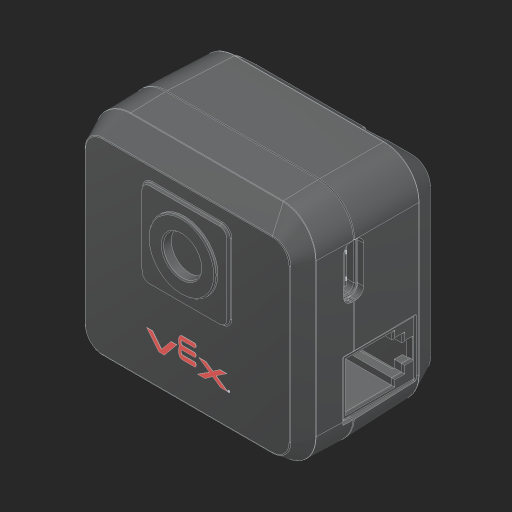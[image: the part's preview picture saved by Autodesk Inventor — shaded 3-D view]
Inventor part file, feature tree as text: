
AUTODESK INVENTOR PART (.ipt)
format: ipt  version: 2023 (Build 270158000, 158)  size: 2,909,696 bytes
history: native  units: in
note: dims shown in document units (in); Inventor stores cm internally (conversion verified against a paired STEP export)
features: other x12, extrude x1, sketch x1
ambient origin geometry x8: Origin, YZ Plane, XZ Plane, XY Plane, X Axis, Y Axis, Z Axis, Center Point
bodies: Solid1 (feature_tree), Solid2 (feature_tree), Solid3 (feature_tree), Solid4 (feature_tree), Solid5 (feature_tree), Solid6 (feature_tree), Solid7 (feature_tree), Solid8 (feature_tree), Solid9 (feature_tree), Solid11 (feature_tree), Solid12 (feature_tree)
feature tree (14):
  extrude  "Extrusion1"  [1 undecoded]
  sketch  "Sketch1"  dims[d19=0.002in d20=0.0in]
  other  "Image1"
  other  "276-7405-002 - OVERMOLD Web_13:1"
  other  "276-4850-014 Rev9_14:1"
  other  "276-4850-014 Rev9_15:1"
  other  "276-7405-003 Web_2:1"
  other  "276-7405-001 Web_3:1"
  other  "276-7405-006 Web_4:1"
  other  "276-7405-006 Web_5:1"
  other  "276-7405-006 Web_6:1"
  other  "276-7405-006 Web_7:1"
  other  "USC2-16FB-NNM1-02_11:1"
  other  "SH-55-41_12:1"
note: 1 required parameter value undecoded (feature->parameter linkage not recoverable at this tier; creation-order binding heuristic only, values carry confidence <= 0.55)
